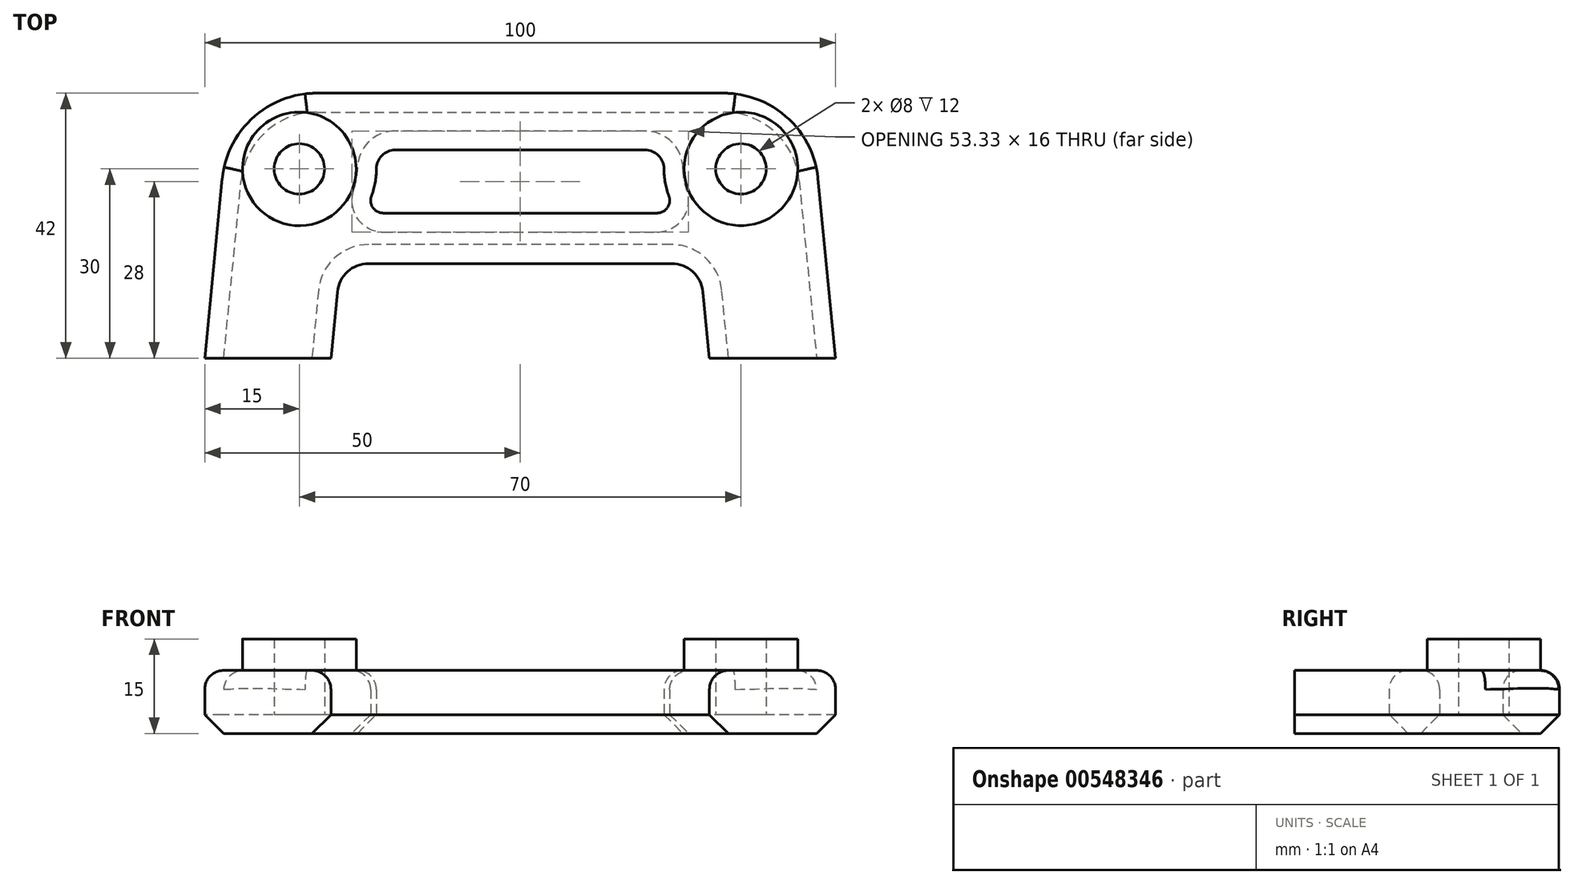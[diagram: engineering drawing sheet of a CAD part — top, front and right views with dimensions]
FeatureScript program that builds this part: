
annotation { "Feature Type Name" : "Feature", "Feature Type Description" : "" }
export const myFeature = defineFeature(function(context is Context, id is Id, definition is map)
    precondition{}
    {
        {
            var Q0;
            Q0=qCreatedBy(makeId("Top.planeOp"),FACE);
            var sketch = newSketch(context, id + "F0", { "sketchPlane" : qUnion([Q0])});
            skLineSegment(sketch, "E0", {"start": v(0, 22) * mm, "end": v(-32.28, 22) * mm});
            skLineSegment(sketch, "E1", {"start": v(-47.2, 8.46) * mm, "end": v(-50, -20) * mm});
            skLineSegment(sketch, "E2", {"start": v(-50, -20) * mm, "end": v(-30, -20) * mm});
            skLineSegment(sketch, "E3", {"start": v(-30, -20) * mm, "end": v(-28.97, -9.51) * mm});
            skLineSegment(sketch, "E4", {"start": v(-24, -5) * mm, "end": v(0, -5) * mm});
            skLineSegment(sketch, "E5", {"start": v(0, 3) * mm, "end": v(-21.7, 3) * mm});
            skLineSegment(sketch, "E6.MirrorCS", {"start": v(0, 22) * mm, "end": v(32.28, 22) * mm});
            skLineSegment(sketch, "E7.MirrorCS", {"start": v(47.2, 8.46) * mm, "end": v(50, -20) * mm});
            skLineSegment(sketch, "E8.MirrorCS", {"start": v(50, -20) * mm, "end": v(30, -20) * mm});
            skLineSegment(sketch, "E9.MirrorCS", {"start": v(30, -20) * mm, "end": v(28.97, -9.51) * mm});
            skLineSegment(sketch, "E10.MirrorCS", {"start": v(24, -5) * mm, "end": v(0, -5) * mm});
            skLineSegment(sketch, "E11.MirrorCS", {"start": v(0, 3) * mm, "end": v(21.7, 3) * mm});
            skPoint(sketch, "E12.visualSharp", {"position": v(-28.53, -5) * mm});
            skArc(sketch, "E12.filletArc", {"start": v(-24, -5) * mm, "mid": v(-27.35, -6.3) * mm, "end": v(-28.97, -9.51) * mm});
            skPoint(sketch, "E13.visualSharp", {"position": v(28.53, -5) * mm});
            skArc(sketch, "E13.filletArc", {"start": v(28.97, -9.51) * mm, "mid": v(27.35, -6.3) * mm, "end": v(24, -5) * mm});
            skCircle(sketch, "E14", {"center": v(-35, 10) * mm, "radius": 4 * mm});
            skCircle(sketch, "E15", {"center": v(35, 10) * mm, "radius": 4 * mm});
            skPoint(sketch, "E16.visualSharp", {"position": v(-45.88, 22) * mm});
            skArc(sketch, "E16.filletArc", {"start": v(-32.28, 22) * mm, "mid": v(-42.36, 18.11) * mm, "end": v(-47.2, 8.46) * mm});
            skPoint(sketch, "E17.visualSharp", {"position": v(45.88, 22) * mm});
            skArc(sketch, "E17.filletArc", {"start": v(47.2, 8.46) * mm, "mid": v(42.36, 18.11) * mm, "end": v(32.28, 22) * mm});
            skArc(sketch, "E18", {"start": v(-23.57, 5.7) * mm, "mid": v(-23, 7.82) * mm, "end": v(-22.8, 10) * mm});
            skArc(sketch, "E19", {"start": v(23.57, 5.7) * mm, "mid": v(23, 7.82) * mm, "end": v(22.8, 10) * mm});
            skArc(sketch, "E20.filletArc", {"start": v(-23.57, 5.7) * mm, "mid": v(-23.35, 3.86) * mm, "end": v(-21.7, 3) * mm});
            skPoint(sketch, "E21.visualSharp", {"position": v(25, 3) * mm});
            skArc(sketch, "E21.filletArc", {"start": v(21.7, 3) * mm, "mid": v(23.35, 3.86) * mm, "end": v(23.57, 5.7) * mm});
            skArc(sketch, "E22", {"start": v(-22.8, 10) * mm, "mid": v(-21.91, 12.12) * mm, "end": v(-19.8, 13) * mm});
            skArc(sketch, "E23", {"start": v(22.8, 10) * mm, "mid": v(21.91, 12.12) * mm, "end": v(19.8, 13) * mm});
            skLineSegment(sketch, "E24", {"start": v(-19.8, 13) * mm, "end": v(19.8, 13) * mm});
            skSolve(sketch);
        }
        {
            var Q0;
            Q0 = qSketchRegion(id + "F0", true);
            extrude(context, id + "F1", {"entities" : qUnion([Q0]), "depth" : 10 * mm, "offsetDistance" : 25 * mm});
        }
        {
            var Q0;
            Q0=makeQuery(id+"F1.opExtrude","CAP_FACE",FACE,{"disambiguationData":[OSD([sQuery(id+"F0.wireOp",EDGE,"E0"),sQuery(id+"F0.wireOp",EDGE,"E1"),sQuery(id+"F0.wireOp",EDGE,"E2"),sQuery(id+"F0.wireOp",EDGE,"E3"),sQuery(id+"F0.wireOp",EDGE,"E4"),sQuery(id+"F0.wireOp",EDGE,"E5"),sQuery(id+"F0.wireOp",EDGE,"E6.MirrorCS"),sQuery(id+"F0.wireOp",EDGE,"E7.MirrorCS"),sQuery(id+"F0.wireOp",EDGE,"E8.MirrorCS"),sQuery(id+"F0.wireOp",EDGE,"E9.MirrorCS"),sQuery(id+"F0.wireOp",EDGE,"E10.MirrorCS"),sQuery(id+"F0.wireOp",EDGE,"E11.MirrorCS"),sQuery(id+"F0.wireOp",EDGE,"E12.filletArc"),sQuery(id+"F0.wireOp",EDGE,"E13.filletArc"),sQuery(id+"F0.wireOp",EDGE,"E14"),sQuery(id+"F0.wireOp",EDGE,"E15"),sQuery(id+"F0.wireOp",EDGE,"E16.filletArc"),sQuery(id+"F0.wireOp",EDGE,"E17.filletArc"),sQuery(id+"F0.wireOp",EDGE,"E18"),sQuery(id+"F0.wireOp",EDGE,"E19"),sQuery(id+"F0.wireOp",EDGE,"E20.filletArc"),sQuery(id+"F0.wireOp",EDGE,"E21.filletArc"),sQuery(id+"F0.wireOp",EDGE,"E22"),sQuery(id+"F0.wireOp",EDGE,"E23"),sQuery(id+"F0.wireOp",EDGE,"E24")])],"isStart":false});
            var sketch = newSketch(context, id + "F2", { "sketchPlane" : qUnion([Q0])});
            skCircle(sketch, "E25", {"center": v(35, 10) * mm, "radius": 9 * mm});
            skCircle(sketch, "E26", {"center": v(35, 10) * mm, "radius": 4 * mm});
            skCircle(sketch, "E27", {"center": v(-35, 10) * mm, "radius": 4 * mm});
            skCircle(sketch, "E28", {"center": v(-35, 10) * mm, "radius": 9 * mm});
            skSolve(sketch);
        }
        {
            var Q0;
            Q0 = qSketchRegion(id + "F2", true);
            extrude(context, id + "F3", {"entities" : qUnion([Q0]), "operationType" : NewBodyOperationType.ADD, "depth" : 5 * mm, "offsetDistance" : 25 * mm});
        }
        {
            var Q0;
            Q0=makeQuery(id+"F1.opExtrude","CAP_FACE",FACE,{"disambiguationData":[OSD([sQuery(id+"F0.wireOp",EDGE,"E0"),sQuery(id+"F0.wireOp",EDGE,"E1"),sQuery(id+"F0.wireOp",EDGE,"E2"),sQuery(id+"F0.wireOp",EDGE,"E3"),sQuery(id+"F0.wireOp",EDGE,"E4"),sQuery(id+"F0.wireOp",EDGE,"E5"),sQuery(id+"F0.wireOp",EDGE,"E6.MirrorCS"),sQuery(id+"F0.wireOp",EDGE,"E7.MirrorCS"),sQuery(id+"F0.wireOp",EDGE,"E8.MirrorCS"),sQuery(id+"F0.wireOp",EDGE,"E9.MirrorCS"),sQuery(id+"F0.wireOp",EDGE,"E10.MirrorCS"),sQuery(id+"F0.wireOp",EDGE,"E11.MirrorCS"),sQuery(id+"F0.wireOp",EDGE,"E12.filletArc"),sQuery(id+"F0.wireOp",EDGE,"E13.filletArc"),sQuery(id+"F0.wireOp",EDGE,"E14"),sQuery(id+"F0.wireOp",EDGE,"E15"),sQuery(id+"F0.wireOp",EDGE,"E16.filletArc"),sQuery(id+"F0.wireOp",EDGE,"E17.filletArc"),sQuery(id+"F0.wireOp",EDGE,"E18"),sQuery(id+"F0.wireOp",EDGE,"E19"),sQuery(id+"F0.wireOp",EDGE,"E20.filletArc"),sQuery(id+"F0.wireOp",EDGE,"E21.filletArc"),sQuery(id+"F0.wireOp",EDGE,"E22"),sQuery(id+"F0.wireOp",EDGE,"E23"),sQuery(id+"F0.wireOp",EDGE,"E24")])],"isStart":true});
            var sketch = newSketch(context, id + "F4", { "sketchPlane" : qUnion([Q0])});
            skCircle(sketch, "E29", {"center": v(35, -10) * mm, "radius": 4 * mm});
            skCircle(sketch, "E30", {"center": v(-35, -10) * mm, "radius": 4 * mm});
            skSolve(sketch);
        }
        {
            var Q0;
            Q0 = qSketchRegion(id + "F4", true);
            extrude(context, id + "F5", {"entities" : qUnion([Q0]), "operationType" : NewBodyOperationType.ADD, "oppositeDirection" : true, "depth" : 3 * mm, "offsetDistance" : 25 * mm});
        }
        {
            var Q0;
            Q0=makeQuery(id+"F1.opExtrude","CAP_EDGE",EDGE,{"disambiguationData":[OSD([sQuery(id+"F0.wireOp",EDGE,"E4"),sQuery(id+"F0.wireOp",EDGE,"E10.MirrorCS")])],"isStart":false});
            var Q1;
            Q1=makeQuery(id+"F1.opExtrude","CAP_EDGE",EDGE,{"disambiguationData":[OSD([sQuery(id+"F0.wireOp",EDGE,"E0"),sQuery(id+"F0.wireOp",EDGE,"E6.MirrorCS")])],"isStart":false});
            var Q2;
            Q2=makeQuery(id+"F1.opExtrude","CAP_EDGE",EDGE,{"disambiguationData":[OSD([sQuery(id+"F0.wireOp",EDGE,"E24")])],"isStart":false});
            fillet(context, id + "F6", {"entities" : qUnion([Q0, Q1, Q2]), "radius" : 3 * mm, "tangentPropagation" : true, "allowEdgeOverflow" : false});
        }
        {
            var Q0;
            Q0=makeQuery(id+"F1.opExtrude","CAP_EDGE",EDGE,{"disambiguationData":[OSD([sQuery(id+"F0.wireOp",EDGE,"E17.filletArc")])],"isStart":true});
            var Q1;
            Q1=makeQuery(id+"F1.opExtrude","CAP_EDGE",EDGE,{"disambiguationData":[OSD([sQuery(id+"F0.wireOp",EDGE,"E24")])],"isStart":true});
            var Q2;
            Q2=makeQuery(id+"F1.opExtrude","CAP_EDGE",EDGE,{"disambiguationData":[OSD([sQuery(id+"F0.wireOp",EDGE,"E4"),sQuery(id+"F0.wireOp",EDGE,"E10.MirrorCS")])],"isStart":true});
            chamfer(context, id + "F7", {"entities" : qUnion([Q0, Q1, Q2]), "width" : 3 * mm, "tangentPropagation" : true});
        }
    });
